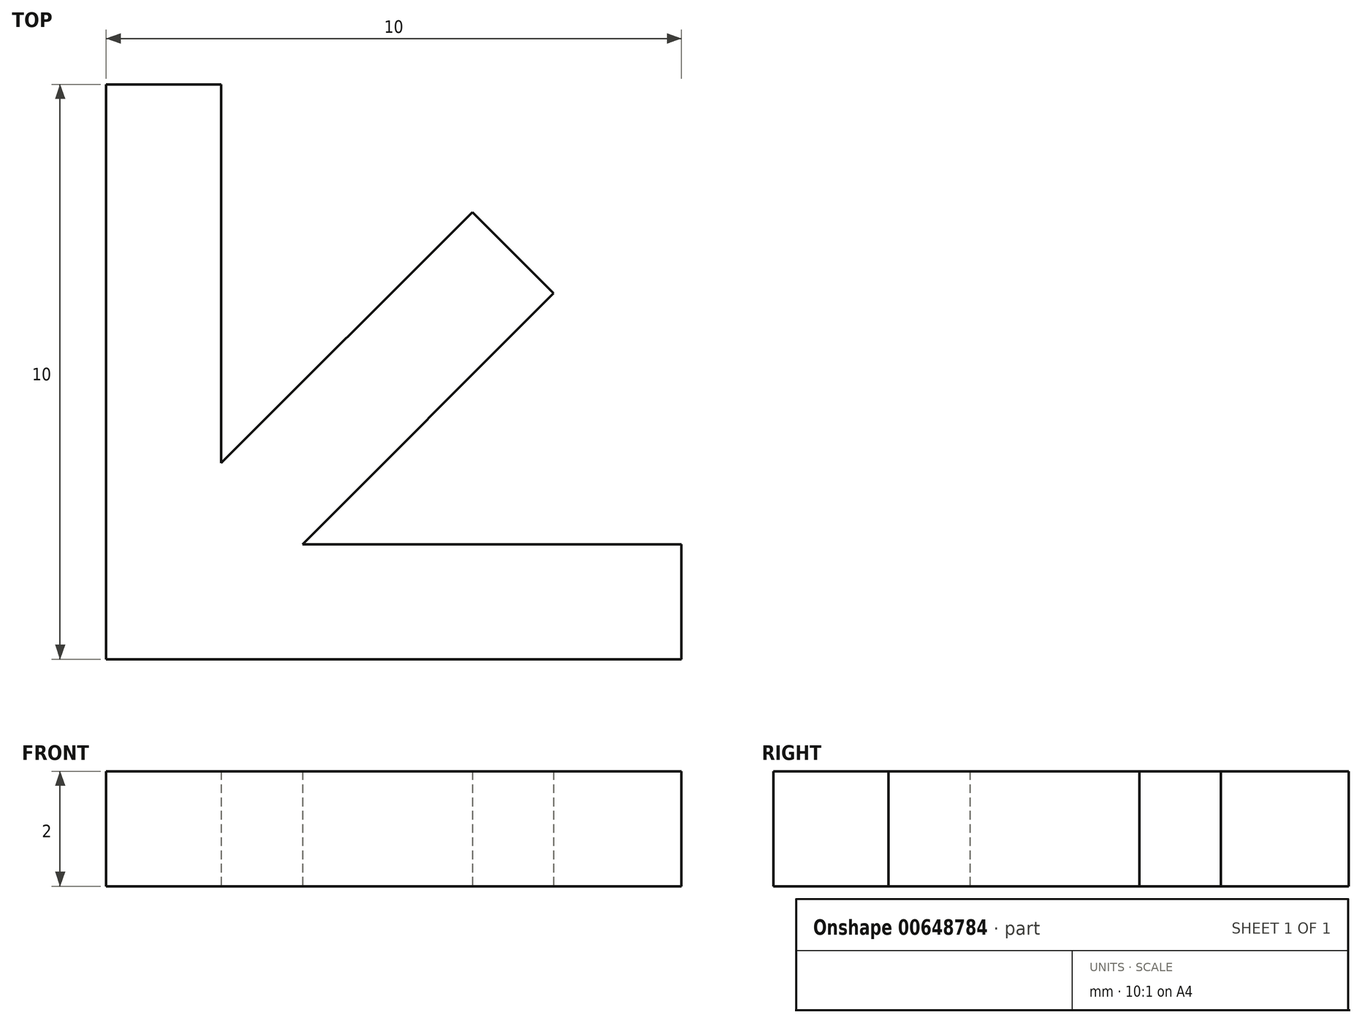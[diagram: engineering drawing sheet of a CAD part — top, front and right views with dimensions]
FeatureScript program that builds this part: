
annotation { "Feature Type Name" : "Feature", "Feature Type Description" : "" }
export const myFeature = defineFeature(function(context is Context, id is Id, definition is map)
    precondition{}
    {
        {
            var Q0;
            Q0=qCreatedBy(makeId("Top.planeOp"),FACE);
            var sketch = newSketch(context, id + "F0", { "sketchPlane" : qUnion([Q0])});
            skLineSegment(sketch, "E0.right", {"start": v(10, 2) * mm, "end": v(10, 0) * mm});
            skLineSegment(sketch, "E1.top", {"start": v(0, 10) * mm, "end": v(2, 10) * mm});
            skLineSegment(sketch, "E1.left", {"start": v(0, 0) * mm, "end": v(0, 10) * mm});
            skLineSegment(sketch, "E1.right", {"start": v(2, 3.41) * mm, "end": v(2, 10) * mm});
            skLineSegment(sketch, "E2", {"start": v(6.36, 7.78) * mm, "end": v(7.78, 6.36) * mm});
            skLineSegment(sketch, "E3", {"start": v(7.78, 6.36) * mm, "end": v(3.41, 2) * mm});
            skLineSegment(sketch, "E4", {"start": v(7.07, 7.07) * mm, "end": v(0, 0) * mm, "construction": true});
            skLineSegment(sketch, "E5.trimOffspring", {"start": v(2, 3.41) * mm, "end": v(6.36, 7.78) * mm});
            skLineSegment(sketch, "E6.trimOffspring", {"start": v(3.41, 2) * mm, "end": v(10, 2) * mm});
            skLineSegment(sketch, "E7", {"start": v(0, 0) * mm, "end": v(10, 0) * mm});
            skSolve(sketch);
        }
        {
            var Q0;
            Q0 = qSketchRegion(id + "F0", true);
            extrude(context, id + "F1", {"entities" : qUnion([Q0]), "depth" : 2 * mm, "offsetDistance" : 25 * mm});
        }
    });
